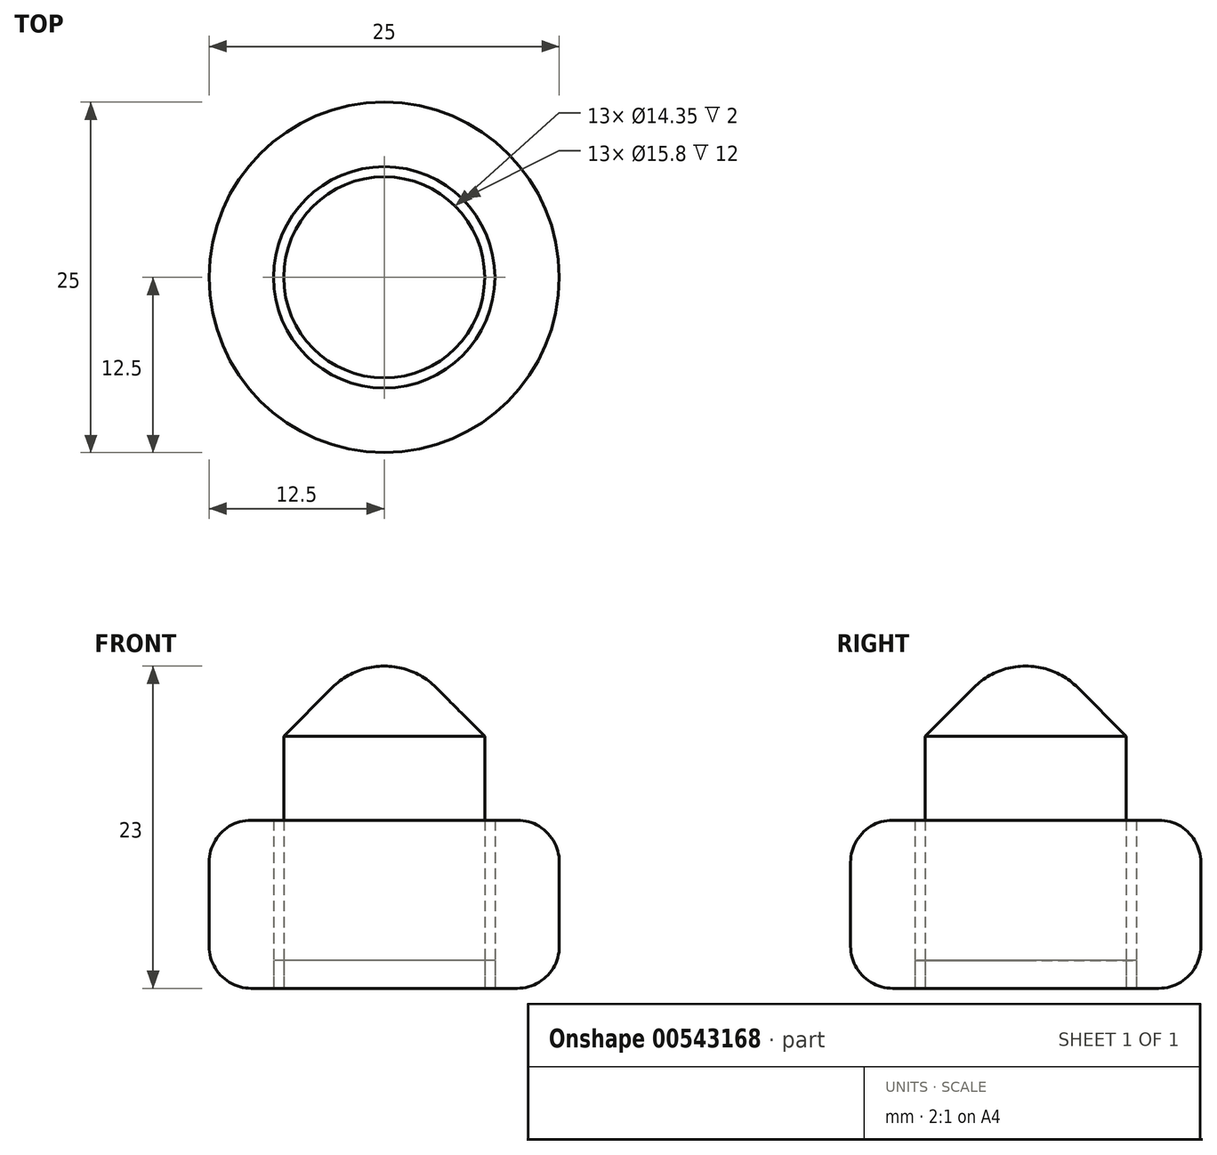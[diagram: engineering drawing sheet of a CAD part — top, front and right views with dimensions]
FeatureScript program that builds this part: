
annotation { "Feature Type Name" : "Feature", "Feature Type Description" : "" }
export const myFeature = defineFeature(function(context is Context, id is Id, definition is map)
    precondition{}
    {
        {
            var Q0;
            Q0=qCreatedBy(makeId("Top.planeOp"),FACE);
            var sketch = newSketch(context, id + "F0", { "sketchPlane" : qUnion([Q0])});
            skCircle(sketch, "E0", {"center": v(0, 0) * mm, "radius": 7.17 * mm});
            skCircle(sketch, "E1", {"center": v(0, 0) * mm, "radius": 7.9 * mm});
            skCircle(sketch, "E2", {"center": v(0, 0) * mm, "radius": 12.5 * mm});
            skSolve(sketch);
        }
        {
            var Q0;
            Q0=makeQuery(id+"F0.imprint","IMPRINT",FACE,{"disambiguationData":[TD([[makeQuery(id+"F0.imprint","IMPRINT",EDGE,{"derivedFrom":sQuery(id+"F0.wireOp",EDGE,"E1")}),-1.0]])]});
            extrude(context, id + "F1", {"entities" : qUnion([Q0]), "depth" : 12 * mm, "offsetDistance" : 25 * mm});
        }
        {
            var Q0;
            Q0=makeQuery(id+"F0.imprint","IMPRINT",FACE,{"disambiguationData":[TD([[makeQuery(id+"F0.imprint","IMPRINT",EDGE,{"derivedFrom":sQuery(id+"F0.wireOp",EDGE,"E0")}),1.0]])]});
            extrude(context, id + "F2", {"entities" : qUnion([Q0]), "depth" : 23 * mm, "offsetDistance" : 25 * mm});
        }
        {
            var Q0;
            Q0=makeQuery(id+"F0.imprint","IMPRINT",FACE,{"disambiguationData":[TD([[makeQuery(id+"F0.imprint","IMPRINT",EDGE,{"derivedFrom":sQuery(id+"F0.wireOp",EDGE,"E0")}),-1.0]])]});
            extrude(context, id + "F3", {"entities" : qUnion([Q0]), "depth" : 2 * mm, "offsetDistance" : 25 * mm});
        }
        {
            var Q0;
            Q0=makeQuery(id+"F1.opExtrude","CAP_EDGE",EDGE,{"disambiguationData":[OSD([sQuery(id+"F0.wireOp",EDGE,"E2")])],"isStart":false});
            var Q1;
            Q1=makeQuery(id+"F1.opExtrude","CAP_EDGE",EDGE,{"disambiguationData":[OSD([sQuery(id+"F0.wireOp",EDGE,"E2")])],"isStart":true});
            fillet(context, id + "F4", {"entities" : qUnion([Q0, Q1]), "radius" : 3 * mm, "tangentPropagation" : true, "allowEdgeOverflow" : false});
        }
        {
            var Q0;
            Q0=makeQuery(id+"F2.opExtrude","CAP_EDGE",EDGE,{"disambiguationData":[OSD([sQuery(id+"F0.wireOp",EDGE,"E0")])],"isStart":false});
            chamfer(context, id + "F5", {"entities" : qUnion([Q0]), "width" : 5 * mm, "tangentPropagation" : true});
        }
        {
            var Q0;
            {var subQ0=sQuery(id+"F0.wireOp",EDGE,"E0");Q0=makeQuery(id+"F5.opChamfer","BLEND_EDGE",EDGE,{"blendedFrom":[makeQuery(id+"F2.opExtrude","CAP_EDGE",EDGE,{"disambiguationData":[OSD([subQ0])],"isStart":false}),makeQuery(id+"F2.opExtrude","CAP_FACE",FACE,{"disambiguationData":[OSD([subQ0])],"isStart":false})],"blendedInto":[makeQuery(id+"F2.opExtrude","CAP_FACE",FACE,{"disambiguationData":[OSD([subQ0])],"isStart":false})]});}
            fillet(context, id + "F6", {"entities" : qUnion([Q0]), "radius" : 5.2 * mm, "tangentPropagation" : true, "allowEdgeOverflow" : false});
        }
    });
